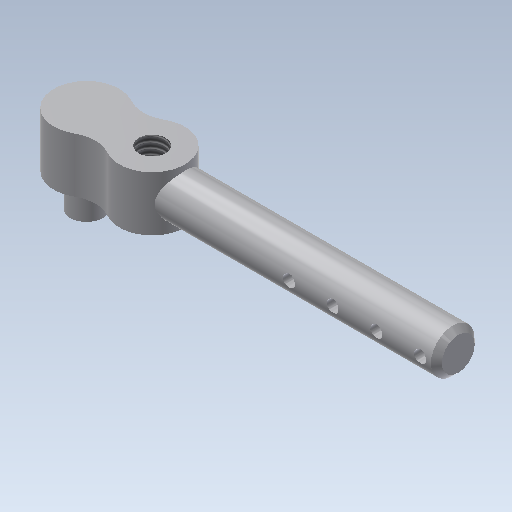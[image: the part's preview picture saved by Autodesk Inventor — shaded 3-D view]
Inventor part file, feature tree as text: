
AUTODESK INVENTOR PART (.ipt)
format: ipt  version: 2020 (Build 240168000, 168)  size: 148,992 bytes
history: native  units: mm
features: extrude x4, sketch x4, hole x1, pattern_linear x1, chamfer x1, projected_geometry x1
ambient origin geometry x8: Origin, YZ Plane, XZ Plane, XY Plane, X Axis, Y Axis, Z Axis, Center Point
bodies: Solid1 (feature_tree)
feature tree (12):
  extrude  "Extrusion1"  Depth=6.0mm
  extrude  "Extrusion2"  Depth=3.0mm
  extrude  "Extrusion3"  Depth=6.0mm
  hole  "Hole1"  [1 undecoded]
  extrude  "Extrusion4"  Depth=31.0mm TaperAngle=0.0deg
  pattern_linear  "Rectangular Pattern1"  Spacing1=3.0mm  [1 undecoded]
  chamfer  "Chamfer1"  Distance=3.0mm
  sketch  "Sketch1"  dims[d0=6.0mm d1=6.0mm]
  sketch  "Sketch2"  dims[d2=6.0mm d3=3.0mm]
  sketch  "Sketch3"  dims[d4=6.0mm d5=6.0mm]
  sketch  "Sketch4"  dims[d6=5.0mm d7=0.0mm d8=4.0mm d9=31.0mm d10=0.0mm d11=3.0mm d12=3.0mm d13=0.0mm d14=10.0mm d15=10.0mm d16=2.459mm d17=6.0mm d18=4.0mm d19=2.0mm d20=90.0deg d21=8.8mm d22=20.594885mm d23=1.1mm d24=1.5mm d25=17.5mm d26=0.0mm d27=40.0mm d29=4.0mm d30=0.5mm d31=2.0mm d32=45.0deg]
  projected_geometry  "Project Cut Edges1"
note: 2 required parameter values undecoded (feature->parameter linkage not recoverable at this tier; creation-order binding heuristic only, values carry confidence <= 0.55)
